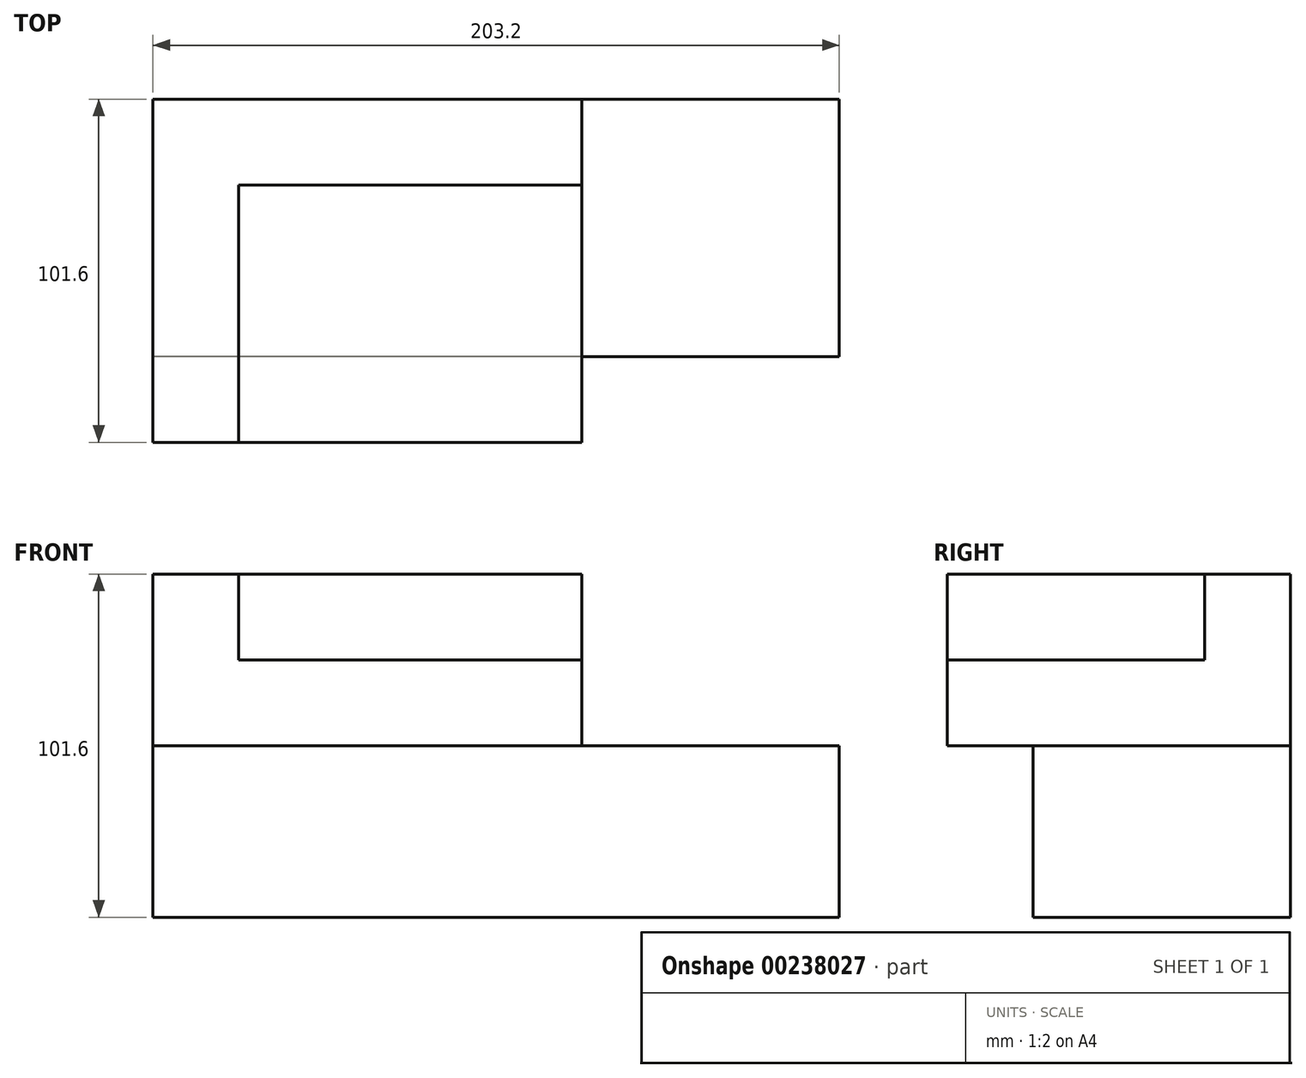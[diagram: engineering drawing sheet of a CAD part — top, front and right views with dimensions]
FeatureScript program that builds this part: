
annotation { "Feature Type Name" : "Feature", "Feature Type Description" : "" }
export const myFeature = defineFeature(function(context is Context, id is Id, definition is map)
    precondition{}
    {
        {
            var Q0;
            Q0=qCreatedBy(makeId("Front.planeOp"),FACE);
            var sketch = newSketch(context, id + "F0", { "sketchPlane" : qUnion([Q0])});
            skLineSegment(sketch, "E0.bottom", {"start": v(-100.46, 81.38) * mm, "end": v(102.74, 81.38) * mm});
            skLineSegment(sketch, "E0.top", {"start": v(-100.46, -20.22) * mm, "end": v(102.74, -20.22) * mm});
            skLineSegment(sketch, "E0.left", {"start": v(-100.46, 81.38) * mm, "end": v(-100.46, -20.22) * mm});
            skLineSegment(sketch, "E0.right", {"start": v(102.74, 81.38) * mm, "end": v(102.74, -20.22) * mm});
            skSolve(sketch);
        }
        {
            var Q0;
            Q0=makeQuery(id+"F0.imprint","IMPRINT",FACE,{"disambiguationData":[TD([[makeQuery(id+"F0.imprint","IMPRINT",EDGE,{"derivedFrom":sQuery(id+"F0.wireOp",EDGE,"E0.bottom")}),-1.0]])]});
            extrude(context, id + "F1", {"entities" : qUnion([Q0]), "depth" : 101.6 * mm});
        }
        {
            var Q0;
            Q0=makeQuery(id+"F1.opExtrude","SWEPT_FACE",FACE,{"disambiguationData":[OSD([sQuery(id+"F0.wireOp",EDGE,"E0.top")])]});
            var sketch = newSketch(context, id + "F2", { "sketchPlane" : qUnion([Q0])});
            skLineSegment(sketch, "E1.bottom", {"start": v(102.74, 101.6) * mm, "end": v(-100.46, 101.6) * mm});
            skLineSegment(sketch, "E1.top", {"start": v(102.74, 76.2) * mm, "end": v(-100.46, 76.2) * mm});
            skLineSegment(sketch, "E1.left", {"start": v(102.74, 101.6) * mm, "end": v(102.74, 76.2) * mm});
            skLineSegment(sketch, "E1.right", {"start": v(-100.46, 101.6) * mm, "end": v(-100.46, 76.2) * mm});
            skSolve(sketch);
        }
        {
            var Q0;
            Q0=makeQuery(id+"F2.imprint","IMPRINT",FACE,{"disambiguationData":[TD([[makeQuery(id+"F2.imprint","IMPRINT",EDGE,{"derivedFrom":sQuery(id+"F2.wireOp",EDGE,"E1.bottom")}),-1.0]])]});
            extrude(context, id + "F3", {"entities" : qUnion([Q0]), "operationType" : NewBodyOperationType.REMOVE, "oppositeDirection" : true, "depth" : 50.8 * mm});
        }
        {
            var Q0;
            Q0=makeQuery(id+"F1.opExtrude","CAP_FACE",FACE,{"disambiguationData":[OSD([sQuery(id+"F0.wireOp",EDGE,"E0.bottom"),sQuery(id+"F0.wireOp",EDGE,"E0.top"),sQuery(id+"F0.wireOp",EDGE,"E0.left"),sQuery(id+"F0.wireOp",EDGE,"E0.right")])],"isStart":true});
            var sketch = newSketch(context, id + "F4", { "sketchPlane" : qUnion([Q0])});
            skLineSegment(sketch, "E2.bottom", {"start": v(-26.54, 81.38) * mm, "end": v(-102.74, 81.38) * mm});
            skLineSegment(sketch, "E2.top", {"start": v(-26.54, 30.58) * mm, "end": v(-102.74, 30.58) * mm});
            skLineSegment(sketch, "E2.left", {"start": v(-26.54, 81.38) * mm, "end": v(-26.54, 30.58) * mm});
            skLineSegment(sketch, "E2.right", {"start": v(-102.74, 81.38) * mm, "end": v(-102.74, 30.58) * mm});
            skSolve(sketch);
        }
        {
            var Q0;
            Q0=makeQuery(id+"F4.imprint","IMPRINT",FACE,{"disambiguationData":[TD([[makeQuery(id+"F4.imprint","IMPRINT",EDGE,{"derivedFrom":sQuery(id+"F4.wireOp",EDGE,"E2.bottom")}),1.0]])]});
            extrude(context, id + "F5", {"entities" : qUnion([Q0]), "operationType" : NewBodyOperationType.REMOVE, "endBound" : BoundingType.THROUGH_ALL, "oppositeDirection" : true, "depth" : 25.4 * mm});
        }
        {
            var Q0;
            Q0=makeQuery(id+"F1.opExtrude","SWEPT_FACE",FACE,{"disambiguationData":[OSD([sQuery(id+"F0.wireOp",EDGE,"E0.bottom")])]});
            var sketch = newSketch(context, id + "F6", { "sketchPlane" : qUnion([Q0])});
            skLineSegment(sketch, "E3.bottom", {"start": v(26.54, -101.6) * mm, "end": v(-75.06, -101.6) * mm});
            skLineSegment(sketch, "E3.top", {"start": v(26.54, -25.4) * mm, "end": v(-75.06, -25.4) * mm});
            skLineSegment(sketch, "E3.left", {"start": v(26.54, -101.6) * mm, "end": v(26.54, -25.4) * mm});
            skLineSegment(sketch, "E3.right", {"start": v(-75.06, -101.6) * mm, "end": v(-75.06, -25.4) * mm});
            skSolve(sketch);
        }
        {
            var Q0;
            Q0=makeQuery(id+"F6.imprint","IMPRINT",FACE,{"disambiguationData":[TD([[makeQuery(id+"F6.imprint","IMPRINT",EDGE,{"derivedFrom":sQuery(id+"F6.wireOp",EDGE,"E3.bottom")}),1.0]])]});
            extrude(context, id + "F7", {"entities" : qUnion([Q0]), "operationType" : NewBodyOperationType.REMOVE, "oppositeDirection" : true, "depth" : 25.4 * mm});
        }
    });
